AUTODESK INVENTOR PART (.ipt)
format: ipt  version: 2023 (Build 270158000, 158)  size: 127,488 bytes
history: native  units: in
note: dims shown in document units (in); Inventor stores cm internally (conversion verified against a paired STEP export)
features: other x6, reference x4, sketch x1
ambient origin geometry x8: Origin, YZ Plane, XZ Plane, XY Plane, X Axis, Y Axis, Z Axis, Center Point
feature tree (11):
  sketch  "Sketch1"
  reference  "Reference1"
  reference  "Reference2"
  reference  "Reference3"
  reference  "Reference4"
  parser-record x1  (decoder bookkeeping rows leaked as tree rows — omitted from the tree; the rows remain in map.json)
  other  "Ladybirdbot.iam"
  other  "M2.5 Hex Spacer 5mm:4"
  other  "M2.5 Hex Spacer 5mm:3"
  other  "M2.5 Hex Spacer 5mm:1"
  other  "M2.5 Hex Spacer 5mm:2"
note: 1 file-system path scrubbed to <path> (originals preserved in map.json)
